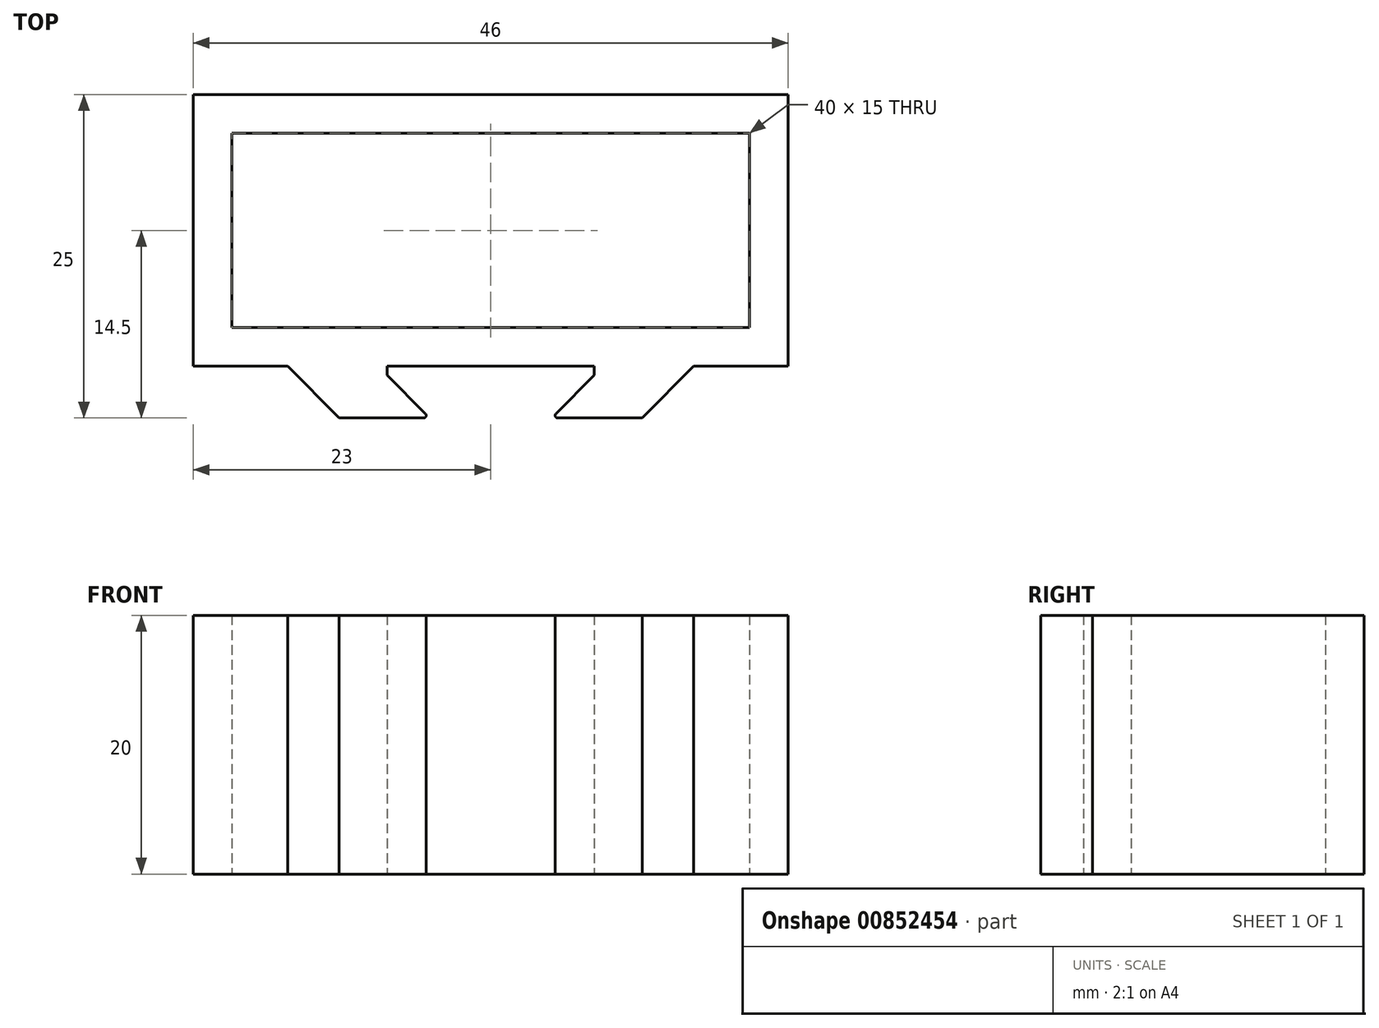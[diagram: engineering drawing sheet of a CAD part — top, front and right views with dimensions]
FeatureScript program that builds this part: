
annotation { "Feature Type Name" : "Feature", "Feature Type Description" : "" }
export const myFeature = defineFeature(function(context is Context, id is Id, definition is map)
    precondition{}
    {
        {
            var Q0;
            Q0=qCreatedBy(makeId("Top.planeOp"),FACE);
            var sketch = newSketch(context, id + "F0", { "sketchPlane" : qUnion([Q0])});
            skLineSegment(sketch, "E0.bottom", {"start": v(-23, 21) * mm, "end": v(23, 21) * mm});
            skLineSegment(sketch, "E0.left", {"start": v(-23, 21) * mm, "end": v(-23, 0) * mm});
            skLineSegment(sketch, "E0.right", {"start": v(23, 21) * mm, "end": v(23, 0) * mm});
            skLineSegment(sketch, "E1.bottom", {"start": v(-20, 18) * mm, "end": v(20, 18) * mm});
            skLineSegment(sketch, "E1.top", {"start": v(-20, 3) * mm, "end": v(20, 3) * mm});
            skLineSegment(sketch, "E1.left", {"start": v(-20, 18) * mm, "end": v(-20, 3) * mm});
            skLineSegment(sketch, "E1.right", {"start": v(20, 18) * mm, "end": v(20, 3) * mm});
            skLineSegment(sketch, "E2", {"start": v(0, 41.18) * mm, "end": v(0, -31.23) * mm, "construction": true});
            skLineSegment(sketch, "E3", {"start": v(-11.7, -4) * mm, "end": v(-5.18, -4) * mm});
            skLineSegment(sketch, "E4.MirrorCS", {"start": v(11.7, -4) * mm, "end": v(5.18, -4) * mm});
            skLineSegment(sketch, "E5", {"start": v(-5.04, -3.66) * mm, "end": v(-8, -0.7) * mm});
            skLineSegment(sketch, "E6", {"start": v(-8, -0.7) * mm, "end": v(-8, 0) * mm});
            skLineSegment(sketch, "E7.MirrorCS", {"start": v(5.04, -3.66) * mm, "end": v(8, -0.7) * mm});
            skLineSegment(sketch, "E8.MirrorCS", {"start": v(8, -0.7) * mm, "end": v(8, 0) * mm});
            skLineSegment(sketch, "E9", {"start": v(-8, 0) * mm, "end": v(8, 0) * mm});
            skPoint(sketch, "E10.visualSharp", {"position": v(-4.7, -4) * mm});
            skArc(sketch, "E10.filletArc", {"start": v(-5.18, -4) * mm, "mid": v(-5, -3.88) * mm, "end": v(-5.04, -3.66) * mm});
            skPoint(sketch, "E11.visualSharp", {"position": v(4.7, -4) * mm});
            skArc(sketch, "E11.filletArc", {"start": v(5.04, -3.66) * mm, "mid": v(5, -3.88) * mm, "end": v(5.18, -4) * mm});
            skLineSegment(sketch, "E12", {"start": v(-23, 0) * mm, "end": v(-15.7, 0) * mm});
            skLineSegment(sketch, "E13", {"start": v(-15.7, 0) * mm, "end": v(-11.7, -4) * mm});
            skLineSegment(sketch, "E14.MirrorCS", {"start": v(15.7, 0) * mm, "end": v(11.7, -4) * mm});
            skLineSegment(sketch, "E15.MirrorCS", {"start": v(23, 0) * mm, "end": v(15.7, 0) * mm});
            skPoint(sketch, "E16.orphan", {"position": v(-23, -4) * mm});
            skPoint(sketch, "E17.orphan", {"position": v(23, -4) * mm});
            skSolve(sketch);
        }
        {
            var Q0;
            Q0=qSketchRegion(id+"F0",true);
            extrude(context, id + "F1", {"entities" : qUnion([Q0]), "flatOperationType" : FlatOperationType.REMOVE, "depth" : 20 * mm, "offsetDistance" : 25 * mm, "domain" : OperationDomain.MODEL, "symmetric" : true});
        }
    });
